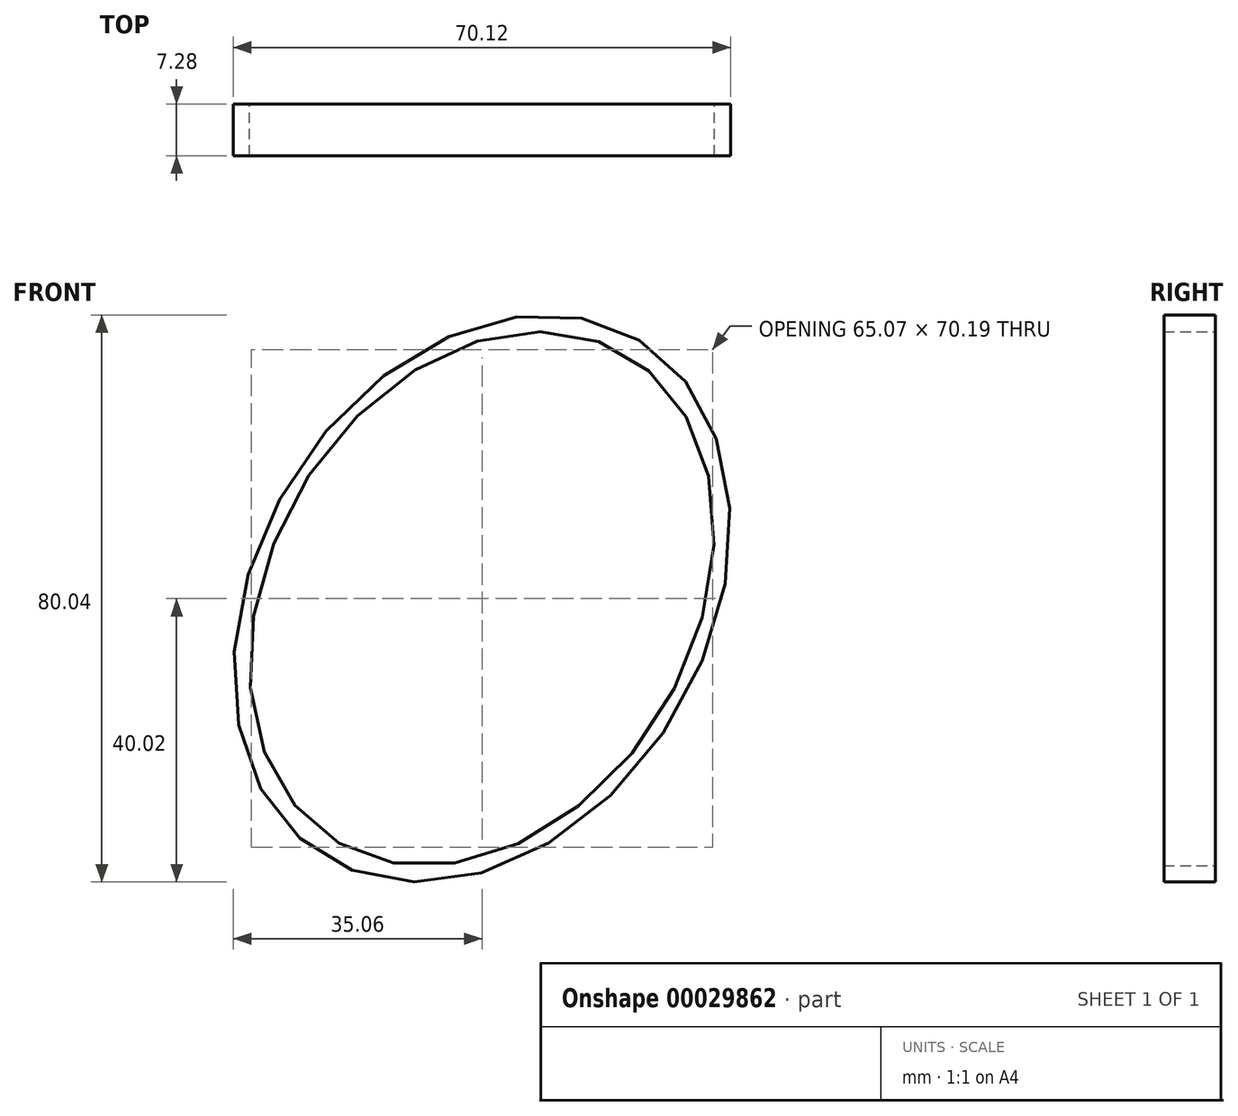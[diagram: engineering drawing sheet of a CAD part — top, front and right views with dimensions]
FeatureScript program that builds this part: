
annotation { "Feature Type Name" : "Feature", "Feature Type Description" : "" }
export const myFeature = defineFeature(function(context is Context, id is Id, definition is map)
    precondition{}
    {
        {
            var Q0;
            Q0=qCreatedBy(makeId("Front.planeOp"),FACE);
            var sketch = newSketch(context, id + "F0", { "sketchPlane" : qUnion([Q0])});
            skEllipse(sketch, "E0", {"center": v(0, 0) * mm, "majorRadius": 29.91 * mm, "minorRadius": 40 * mm, "majorAxis": v(-0.86, 0.5)});
            skEllipse(sketch, "E1", {"center": v(0, 0) * mm, "majorRadius": 42.68 * mm, "minorRadius": 31.76 * mm, "majorAxis": v(0.52, 0.85)});
            skSolve(sketch);
        }
        {
            var Q0;
            Q0 = qSketchRegion(id + "F0", true);
            extrude(context, id + "F1", {"entities" : qUnion([Q0]), "depth" : 7.28 * mm});
        }
    });
